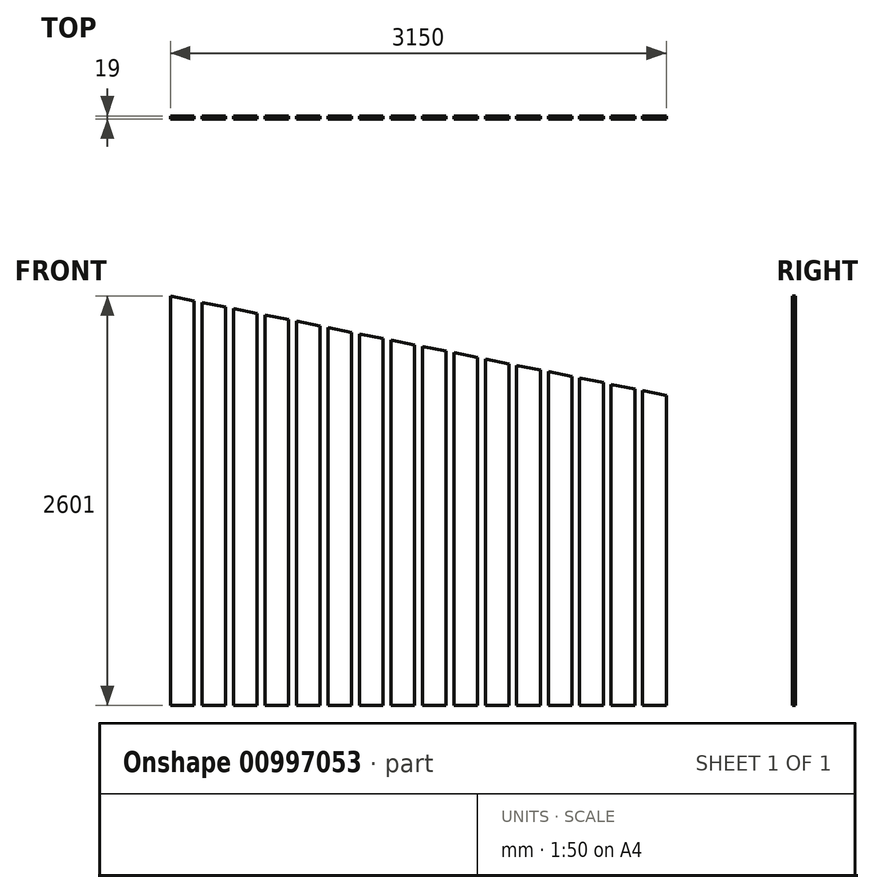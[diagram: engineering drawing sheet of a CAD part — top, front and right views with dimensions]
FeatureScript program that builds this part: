
annotation { "Feature Type Name" : "Feature", "Feature Type Description" : "" }
export const myFeature = defineFeature(function(context is Context, id is Id, definition is map)
    precondition{}
    {
        {
            var Q0;
            Q0=qCreatedBy(makeId("Top.planeOp"),FACE);
            var sketch = newSketch(context, id + "F0", { "sketchPlane" : qUnion([Q0])});
            skLineSegment(sketch, "E0.bottom", {"start": v(0, 0) * mm, "end": v(-150, 0) * mm});
            skLineSegment(sketch, "E0.top", {"start": v(0, 19) * mm, "end": v(-150, 19) * mm});
            skLineSegment(sketch, "E0.left", {"start": v(0, 0) * mm, "end": v(0, 19) * mm});
            skLineSegment(sketch, "E0.right", {"start": v(-150, 0) * mm, "end": v(-150, 19) * mm});
            skSolve(sketch);
        }
        {
            var Q0;
            Q0=makeQuery(id+"F0.imprint","IMPRINT",FACE,{"disambiguationData":[TD([[makeQuery(id+"F0.imprint","IMPRINT",EDGE,{"derivedFrom":sQuery(id+"F0.wireOp",EDGE,"E0.bottom")}),-1.0]])]});
            extrude(context, id + "F1", {"entities" : qUnion([Q0]), "depth" : 2000 * mm, "offsetDistance" : 25 * mm});
        }
        {
            var Q0;
            Q0=makeQuery(id+"F1.opExtrude","CAP_EDGE",EDGE,{"disambiguationData":[OSD([sQuery(id+"F0.wireOp",EDGE,"E0.left")])],"isStart":false});
            chamfer(context, id + "F2", {"entities" : qUnion([Q0]), "chamferType" : ChamferType.OFFSET_ANGLE, "width" : 150 * mm, "oppositeDirection" : false, "angle" : 11.3 * degree, "tangentPropagation" : true});
        }
        {
            var Q0;
            Q0=makeQuery(id+"F1.opExtrude","SWEPT_BODY",BODY,{"disambiguationData":[OSD([sQuery(id+"F0.wireOp",EDGE,"E0.bottom"),sQuery(id+"F0.wireOp",EDGE,"E0.top"),sQuery(id+"F0.wireOp",EDGE,"E0.left"),sQuery(id+"F0.wireOp",EDGE,"E0.right")])]});
            transform(context, id + "F3", {"entities" : qUnion([Q0]), "transformType" : TransformType.TRANSLATION_3D, "dx" : -200 * mm, "dy" : 0 * mm, "dz" : 40 * mm, "makeCopy" : true});
        }
        {
            var Q0;
            Q0=makeQuery(id+"F3.opPattern","COPY",BODY,{"derivedFrom":makeQuery(id+"F1.opExtrude","SWEPT_BODY",BODY,{"disambiguationData":[OSD([sQuery(id+"F0.wireOp",EDGE,"E0.bottom"),sQuery(id+"F0.wireOp",EDGE,"E0.top"),sQuery(id+"F0.wireOp",EDGE,"E0.left"),sQuery(id+"F0.wireOp",EDGE,"E0.right")])]}),"instanceName":"1"});
            transform(context, id + "F4", {"entities" : qUnion([Q0]), "transformType" : TransformType.TRANSLATION_3D, "dx" : -200 * mm, "dy" : 0 * mm, "dz" : 41 * mm, "makeCopy" : true});
        }
        {
            var Q0;
            Q0=makeQuery(id+"F4.opPattern","COPY",BODY,{"derivedFrom":makeQuery(id+"F3.opPattern","COPY",BODY,{"derivedFrom":makeQuery(id+"F1.opExtrude","SWEPT_BODY",BODY,{"disambiguationData":[OSD([sQuery(id+"F0.wireOp",EDGE,"E0.bottom"),sQuery(id+"F0.wireOp",EDGE,"E0.top"),sQuery(id+"F0.wireOp",EDGE,"E0.left"),sQuery(id+"F0.wireOp",EDGE,"E0.right")])]}),"instanceName":"1"}),"instanceName":"1"});
            transform(context, id + "F5", {"entities" : qUnion([Q0]), "transformType" : TransformType.TRANSLATION_3D, "dx" : -200 * mm, "dy" : 0 * mm, "dz" : 40 * mm, "makeCopy" : true});
        }
        {
            var Q0;
            Q0=makeQuery(id+"F5.opPattern","COPY",BODY,{"derivedFrom":makeQuery(id+"F4.opPattern","COPY",BODY,{"derivedFrom":makeQuery(id+"F3.opPattern","COPY",BODY,{"derivedFrom":makeQuery(id+"F1.opExtrude","SWEPT_BODY",BODY,{"disambiguationData":[OSD([sQuery(id+"F0.wireOp",EDGE,"E0.bottom"),sQuery(id+"F0.wireOp",EDGE,"E0.top"),sQuery(id+"F0.wireOp",EDGE,"E0.left"),sQuery(id+"F0.wireOp",EDGE,"E0.right")])]}),"instanceName":"1"}),"instanceName":"1"}),"instanceName":"1"});
            transform(context, id + "F6", {"entities" : qUnion([Q0]), "transformType" : TransformType.TRANSLATION_3D, "dx" : -200 * mm, "dy" : 0 * mm, "dz" : 40 * mm, "makeCopy" : true});
        }
        {
            var Q0;
            Q0=makeQuery(id+"F6.opPattern","COPY",BODY,{"derivedFrom":makeQuery(id+"F5.opPattern","COPY",BODY,{"derivedFrom":makeQuery(id+"F4.opPattern","COPY",BODY,{"derivedFrom":makeQuery(id+"F3.opPattern","COPY",BODY,{"derivedFrom":makeQuery(id+"F1.opExtrude","SWEPT_BODY",BODY,{"disambiguationData":[OSD([sQuery(id+"F0.wireOp",EDGE,"E0.bottom"),sQuery(id+"F0.wireOp",EDGE,"E0.top"),sQuery(id+"F0.wireOp",EDGE,"E0.left"),sQuery(id+"F0.wireOp",EDGE,"E0.right")])]}),"instanceName":"1"}),"instanceName":"1"}),"instanceName":"1"}),"instanceName":"1"});
            transform(context, id + "F7", {"entities" : qUnion([Q0]), "transformType" : TransformType.TRANSLATION_3D, "dx" : -200 * mm, "dy" : 0 * mm, "dz" : 40 * mm, "makeCopy" : true});
        }
        {
            var Q0;
            Q0=makeQuery(id+"F7.opPattern","COPY",BODY,{"derivedFrom":makeQuery(id+"F6.opPattern","COPY",BODY,{"derivedFrom":makeQuery(id+"F5.opPattern","COPY",BODY,{"derivedFrom":makeQuery(id+"F4.opPattern","COPY",BODY,{"derivedFrom":makeQuery(id+"F3.opPattern","COPY",BODY,{"derivedFrom":makeQuery(id+"F1.opExtrude","SWEPT_BODY",BODY,{"disambiguationData":[OSD([sQuery(id+"F0.wireOp",EDGE,"E0.bottom"),sQuery(id+"F0.wireOp",EDGE,"E0.top"),sQuery(id+"F0.wireOp",EDGE,"E0.left"),sQuery(id+"F0.wireOp",EDGE,"E0.right")])]}),"instanceName":"1"}),"instanceName":"1"}),"instanceName":"1"}),"instanceName":"1"}),"instanceName":"1"});
            transform(context, id + "F8", {"entities" : qUnion([Q0]), "transformType" : TransformType.TRANSLATION_3D, "dx" : -200 * mm, "dy" : 0 * mm, "dz" : 40 * mm, "makeCopy" : true});
        }
        {
            var Q0;
            Q0=makeQuery(id+"F8.opPattern","COPY",BODY,{"derivedFrom":makeQuery(id+"F7.opPattern","COPY",BODY,{"derivedFrom":makeQuery(id+"F6.opPattern","COPY",BODY,{"derivedFrom":makeQuery(id+"F5.opPattern","COPY",BODY,{"derivedFrom":makeQuery(id+"F4.opPattern","COPY",BODY,{"derivedFrom":makeQuery(id+"F3.opPattern","COPY",BODY,{"derivedFrom":makeQuery(id+"F1.opExtrude","SWEPT_BODY",BODY,{"disambiguationData":[OSD([sQuery(id+"F0.wireOp",EDGE,"E0.bottom"),sQuery(id+"F0.wireOp",EDGE,"E0.top"),sQuery(id+"F0.wireOp",EDGE,"E0.left"),sQuery(id+"F0.wireOp",EDGE,"E0.right")])]}),"instanceName":"1"}),"instanceName":"1"}),"instanceName":"1"}),"instanceName":"1"}),"instanceName":"1"}),"instanceName":"1"});
            transform(context, id + "F9", {"entities" : qUnion([Q0]), "transformType" : TransformType.TRANSLATION_3D, "dx" : -200 * mm, "dy" : 0 * mm, "dz" : 40 * mm, "makeCopy" : true});
        }
        {
            var Q0;
            Q0=makeQuery(id+"F9.opPattern","COPY",BODY,{"derivedFrom":makeQuery(id+"F8.opPattern","COPY",BODY,{"derivedFrom":makeQuery(id+"F7.opPattern","COPY",BODY,{"derivedFrom":makeQuery(id+"F6.opPattern","COPY",BODY,{"derivedFrom":makeQuery(id+"F5.opPattern","COPY",BODY,{"derivedFrom":makeQuery(id+"F4.opPattern","COPY",BODY,{"derivedFrom":makeQuery(id+"F3.opPattern","COPY",BODY,{"derivedFrom":makeQuery(id+"F1.opExtrude","SWEPT_BODY",BODY,{"disambiguationData":[OSD([sQuery(id+"F0.wireOp",EDGE,"E0.bottom"),sQuery(id+"F0.wireOp",EDGE,"E0.top"),sQuery(id+"F0.wireOp",EDGE,"E0.left"),sQuery(id+"F0.wireOp",EDGE,"E0.right")])]}),"instanceName":"1"}),"instanceName":"1"}),"instanceName":"1"}),"instanceName":"1"}),"instanceName":"1"}),"instanceName":"1"}),"instanceName":"1"});
            transform(context, id + "F10", {"entities" : qUnion([Q0]), "transformType" : TransformType.TRANSLATION_3D, "dx" : -200 * mm, "dy" : 0 * mm, "dz" : 40 * mm, "makeCopy" : true});
        }
        {
            var Q0;
            Q0=makeQuery(id+"F10.opPattern","COPY",BODY,{"derivedFrom":makeQuery(id+"F9.opPattern","COPY",BODY,{"derivedFrom":makeQuery(id+"F8.opPattern","COPY",BODY,{"derivedFrom":makeQuery(id+"F7.opPattern","COPY",BODY,{"derivedFrom":makeQuery(id+"F6.opPattern","COPY",BODY,{"derivedFrom":makeQuery(id+"F5.opPattern","COPY",BODY,{"derivedFrom":makeQuery(id+"F4.opPattern","COPY",BODY,{"derivedFrom":makeQuery(id+"F3.opPattern","COPY",BODY,{"derivedFrom":makeQuery(id+"F1.opExtrude","SWEPT_BODY",BODY,{"disambiguationData":[OSD([sQuery(id+"F0.wireOp",EDGE,"E0.bottom"),sQuery(id+"F0.wireOp",EDGE,"E0.top"),sQuery(id+"F0.wireOp",EDGE,"E0.left"),sQuery(id+"F0.wireOp",EDGE,"E0.right")])]}),"instanceName":"1"}),"instanceName":"1"}),"instanceName":"1"}),"instanceName":"1"}),"instanceName":"1"}),"instanceName":"1"}),"instanceName":"1"}),"instanceName":"1"});
            transform(context, id + "F11", {"entities" : qUnion([Q0]), "transformType" : TransformType.TRANSLATION_3D, "dx" : -200 * mm, "dy" : 0 * mm, "dz" : 40 * mm, "makeCopy" : true});
        }
        {
            var Q0;
            Q0=makeQuery(id+"F11.opPattern","COPY",BODY,{"derivedFrom":makeQuery(id+"F10.opPattern","COPY",BODY,{"derivedFrom":makeQuery(id+"F9.opPattern","COPY",BODY,{"derivedFrom":makeQuery(id+"F8.opPattern","COPY",BODY,{"derivedFrom":makeQuery(id+"F7.opPattern","COPY",BODY,{"derivedFrom":makeQuery(id+"F6.opPattern","COPY",BODY,{"derivedFrom":makeQuery(id+"F5.opPattern","COPY",BODY,{"derivedFrom":makeQuery(id+"F4.opPattern","COPY",BODY,{"derivedFrom":makeQuery(id+"F3.opPattern","COPY",BODY,{"derivedFrom":makeQuery(id+"F1.opExtrude","SWEPT_BODY",BODY,{"disambiguationData":[OSD([sQuery(id+"F0.wireOp",EDGE,"E0.bottom"),sQuery(id+"F0.wireOp",EDGE,"E0.top"),sQuery(id+"F0.wireOp",EDGE,"E0.left"),sQuery(id+"F0.wireOp",EDGE,"E0.right")])]}),"instanceName":"1"}),"instanceName":"1"}),"instanceName":"1"}),"instanceName":"1"}),"instanceName":"1"}),"instanceName":"1"}),"instanceName":"1"}),"instanceName":"1"}),"instanceName":"1"});
            transform(context, id + "F12", {"entities" : qUnion([Q0]), "transformType" : TransformType.TRANSLATION_3D, "dx" : -200 * mm, "dy" : 0 * mm, "dz" : 40 * mm, "makeCopy" : true});
        }
        {
            var Q0;
            Q0=makeQuery(id+"F12.opPattern","COPY",BODY,{"derivedFrom":makeQuery(id+"F11.opPattern","COPY",BODY,{"derivedFrom":makeQuery(id+"F10.opPattern","COPY",BODY,{"derivedFrom":makeQuery(id+"F9.opPattern","COPY",BODY,{"derivedFrom":makeQuery(id+"F8.opPattern","COPY",BODY,{"derivedFrom":makeQuery(id+"F7.opPattern","COPY",BODY,{"derivedFrom":makeQuery(id+"F6.opPattern","COPY",BODY,{"derivedFrom":makeQuery(id+"F5.opPattern","COPY",BODY,{"derivedFrom":makeQuery(id+"F4.opPattern","COPY",BODY,{"derivedFrom":makeQuery(id+"F3.opPattern","COPY",BODY,{"derivedFrom":makeQuery(id+"F1.opExtrude","SWEPT_BODY",BODY,{"disambiguationData":[OSD([sQuery(id+"F0.wireOp",EDGE,"E0.bottom"),sQuery(id+"F0.wireOp",EDGE,"E0.top"),sQuery(id+"F0.wireOp",EDGE,"E0.left"),sQuery(id+"F0.wireOp",EDGE,"E0.right")])]}),"instanceName":"1"}),"instanceName":"1"}),"instanceName":"1"}),"instanceName":"1"}),"instanceName":"1"}),"instanceName":"1"}),"instanceName":"1"}),"instanceName":"1"}),"instanceName":"1"}),"instanceName":"1"});
            transform(context, id + "F13", {"entities" : qUnion([Q0]), "transformType" : TransformType.TRANSLATION_3D, "dx" : -200 * mm, "dy" : 0 * mm, "dz" : 40 * mm, "makeCopy" : true});
        }
        {
            var Q0;
            Q0=makeQuery(id+"F3.opPattern","COPY",FACE,{"derivedFrom":makeQuery(id+"F1.opExtrude","CAP_FACE",FACE,{"disambiguationData":[OSD([sQuery(id+"F0.wireOp",EDGE,"E0.bottom"),sQuery(id+"F0.wireOp",EDGE,"E0.top"),sQuery(id+"F0.wireOp",EDGE,"E0.left"),sQuery(id+"F0.wireOp",EDGE,"E0.right")])],"isStart":true}),"instanceName":"1"});
            extrude(context, id + "F14", {"entities" : qUnion([Q0]), "operationType" : NewBodyOperationType.ADD, "depth" : 40 * mm, "offsetDistance" : 25 * mm});
        }
        {
            var Q0;
            Q0=makeQuery(id+"F5.opPattern","COPY",FACE,{"derivedFrom":makeQuery(id+"F4.opPattern","COPY",FACE,{"derivedFrom":makeQuery(id+"F3.opPattern","COPY",FACE,{"derivedFrom":makeQuery(id+"F1.opExtrude","CAP_FACE",FACE,{"disambiguationData":[OSD([sQuery(id+"F0.wireOp",EDGE,"E0.bottom"),sQuery(id+"F0.wireOp",EDGE,"E0.top"),sQuery(id+"F0.wireOp",EDGE,"E0.left"),sQuery(id+"F0.wireOp",EDGE,"E0.right")])],"isStart":true}),"instanceName":"1"}),"instanceName":"1"}),"instanceName":"1"});
            extrude(context, id + "F15", {"entities" : qUnion([Q0]), "operationType" : NewBodyOperationType.ADD, "depth" : 120 * mm, "offsetDistance" : 25 * mm});
        }
        {
            var Q0;
            Q0=makeQuery(id+"F4.opPattern","COPY",FACE,{"derivedFrom":makeQuery(id+"F3.opPattern","COPY",FACE,{"derivedFrom":makeQuery(id+"F1.opExtrude","CAP_FACE",FACE,{"disambiguationData":[OSD([sQuery(id+"F0.wireOp",EDGE,"E0.bottom"),sQuery(id+"F0.wireOp",EDGE,"E0.top"),sQuery(id+"F0.wireOp",EDGE,"E0.left"),sQuery(id+"F0.wireOp",EDGE,"E0.right")])],"isStart":true}),"instanceName":"1"}),"instanceName":"1"});
            extrude(context, id + "F16", {"entities" : qUnion([Q0]), "operationType" : NewBodyOperationType.ADD, "depth" : 80 * mm, "offsetDistance" : 25 * mm});
        }
        {
            var Q0;
            Q0=makeQuery(id+"F6.opPattern","COPY",FACE,{"derivedFrom":makeQuery(id+"F5.opPattern","COPY",FACE,{"derivedFrom":makeQuery(id+"F4.opPattern","COPY",FACE,{"derivedFrom":makeQuery(id+"F3.opPattern","COPY",FACE,{"derivedFrom":makeQuery(id+"F1.opExtrude","CAP_FACE",FACE,{"disambiguationData":[OSD([sQuery(id+"F0.wireOp",EDGE,"E0.bottom"),sQuery(id+"F0.wireOp",EDGE,"E0.top"),sQuery(id+"F0.wireOp",EDGE,"E0.left"),sQuery(id+"F0.wireOp",EDGE,"E0.right")])],"isStart":true}),"instanceName":"1"}),"instanceName":"1"}),"instanceName":"1"}),"instanceName":"1"});
            extrude(context, id + "F17", {"entities" : qUnion([Q0]), "operationType" : NewBodyOperationType.ADD, "depth" : 160 * mm, "offsetDistance" : 25 * mm});
        }
        {
            var Q0;
            Q0=makeQuery(id+"F7.opPattern","COPY",FACE,{"derivedFrom":makeQuery(id+"F6.opPattern","COPY",FACE,{"derivedFrom":makeQuery(id+"F5.opPattern","COPY",FACE,{"derivedFrom":makeQuery(id+"F4.opPattern","COPY",FACE,{"derivedFrom":makeQuery(id+"F3.opPattern","COPY",FACE,{"derivedFrom":makeQuery(id+"F1.opExtrude","CAP_FACE",FACE,{"disambiguationData":[OSD([sQuery(id+"F0.wireOp",EDGE,"E0.bottom"),sQuery(id+"F0.wireOp",EDGE,"E0.top"),sQuery(id+"F0.wireOp",EDGE,"E0.left"),sQuery(id+"F0.wireOp",EDGE,"E0.right")])],"isStart":true}),"instanceName":"1"}),"instanceName":"1"}),"instanceName":"1"}),"instanceName":"1"}),"instanceName":"1"});
            extrude(context, id + "F18", {"entities" : qUnion([Q0]), "operationType" : NewBodyOperationType.ADD, "depth" : 200 * mm, "offsetDistance" : 25 * mm});
        }
        {
            var Q0;
            Q0=makeQuery(id+"F8.opPattern","COPY",FACE,{"derivedFrom":makeQuery(id+"F7.opPattern","COPY",FACE,{"derivedFrom":makeQuery(id+"F6.opPattern","COPY",FACE,{"derivedFrom":makeQuery(id+"F5.opPattern","COPY",FACE,{"derivedFrom":makeQuery(id+"F4.opPattern","COPY",FACE,{"derivedFrom":makeQuery(id+"F3.opPattern","COPY",FACE,{"derivedFrom":makeQuery(id+"F1.opExtrude","CAP_FACE",FACE,{"disambiguationData":[OSD([sQuery(id+"F0.wireOp",EDGE,"E0.bottom"),sQuery(id+"F0.wireOp",EDGE,"E0.top"),sQuery(id+"F0.wireOp",EDGE,"E0.left"),sQuery(id+"F0.wireOp",EDGE,"E0.right")])],"isStart":true}),"instanceName":"1"}),"instanceName":"1"}),"instanceName":"1"}),"instanceName":"1"}),"instanceName":"1"}),"instanceName":"1"});
            extrude(context, id + "F19", {"entities" : qUnion([Q0]), "operationType" : NewBodyOperationType.ADD, "depth" : 240 * mm, "offsetDistance" : 25 * mm});
        }
        {
            var Q0;
            Q0=makeQuery(id+"F9.opPattern","COPY",FACE,{"derivedFrom":makeQuery(id+"F8.opPattern","COPY",FACE,{"derivedFrom":makeQuery(id+"F7.opPattern","COPY",FACE,{"derivedFrom":makeQuery(id+"F6.opPattern","COPY",FACE,{"derivedFrom":makeQuery(id+"F5.opPattern","COPY",FACE,{"derivedFrom":makeQuery(id+"F4.opPattern","COPY",FACE,{"derivedFrom":makeQuery(id+"F3.opPattern","COPY",FACE,{"derivedFrom":makeQuery(id+"F1.opExtrude","CAP_FACE",FACE,{"disambiguationData":[OSD([sQuery(id+"F0.wireOp",EDGE,"E0.bottom"),sQuery(id+"F0.wireOp",EDGE,"E0.top"),sQuery(id+"F0.wireOp",EDGE,"E0.left"),sQuery(id+"F0.wireOp",EDGE,"E0.right")])],"isStart":true}),"instanceName":"1"}),"instanceName":"1"}),"instanceName":"1"}),"instanceName":"1"}),"instanceName":"1"}),"instanceName":"1"}),"instanceName":"1"});
            extrude(context, id + "F20", {"entities" : qUnion([Q0]), "operationType" : NewBodyOperationType.ADD, "depth" : 280 * mm, "offsetDistance" : 25 * mm});
        }
        {
            var Q0;
            Q0=makeQuery(id+"F10.opPattern","COPY",FACE,{"derivedFrom":makeQuery(id+"F9.opPattern","COPY",FACE,{"derivedFrom":makeQuery(id+"F8.opPattern","COPY",FACE,{"derivedFrom":makeQuery(id+"F7.opPattern","COPY",FACE,{"derivedFrom":makeQuery(id+"F6.opPattern","COPY",FACE,{"derivedFrom":makeQuery(id+"F5.opPattern","COPY",FACE,{"derivedFrom":makeQuery(id+"F4.opPattern","COPY",FACE,{"derivedFrom":makeQuery(id+"F3.opPattern","COPY",FACE,{"derivedFrom":makeQuery(id+"F1.opExtrude","CAP_FACE",FACE,{"disambiguationData":[OSD([sQuery(id+"F0.wireOp",EDGE,"E0.bottom"),sQuery(id+"F0.wireOp",EDGE,"E0.top"),sQuery(id+"F0.wireOp",EDGE,"E0.left"),sQuery(id+"F0.wireOp",EDGE,"E0.right")])],"isStart":true}),"instanceName":"1"}),"instanceName":"1"}),"instanceName":"1"}),"instanceName":"1"}),"instanceName":"1"}),"instanceName":"1"}),"instanceName":"1"}),"instanceName":"1"});
            extrude(context, id + "F21", {"entities" : qUnion([Q0]), "operationType" : NewBodyOperationType.ADD, "depth" : 320 * mm, "offsetDistance" : 25 * mm});
        }
        {
            var Q0;
            Q0=makeQuery(id+"F11.opPattern","COPY",FACE,{"derivedFrom":makeQuery(id+"F10.opPattern","COPY",FACE,{"derivedFrom":makeQuery(id+"F9.opPattern","COPY",FACE,{"derivedFrom":makeQuery(id+"F8.opPattern","COPY",FACE,{"derivedFrom":makeQuery(id+"F7.opPattern","COPY",FACE,{"derivedFrom":makeQuery(id+"F6.opPattern","COPY",FACE,{"derivedFrom":makeQuery(id+"F5.opPattern","COPY",FACE,{"derivedFrom":makeQuery(id+"F4.opPattern","COPY",FACE,{"derivedFrom":makeQuery(id+"F3.opPattern","COPY",FACE,{"derivedFrom":makeQuery(id+"F1.opExtrude","CAP_FACE",FACE,{"disambiguationData":[OSD([sQuery(id+"F0.wireOp",EDGE,"E0.bottom"),sQuery(id+"F0.wireOp",EDGE,"E0.top"),sQuery(id+"F0.wireOp",EDGE,"E0.left"),sQuery(id+"F0.wireOp",EDGE,"E0.right")])],"isStart":true}),"instanceName":"1"}),"instanceName":"1"}),"instanceName":"1"}),"instanceName":"1"}),"instanceName":"1"}),"instanceName":"1"}),"instanceName":"1"}),"instanceName":"1"}),"instanceName":"1"});
            extrude(context, id + "F22", {"entities" : qUnion([Q0]), "operationType" : NewBodyOperationType.ADD, "depth" : 360 * mm, "offsetDistance" : 25 * mm});
        }
        {
            var Q0;
            Q0=makeQuery(id+"F12.opPattern","COPY",FACE,{"derivedFrom":makeQuery(id+"F11.opPattern","COPY",FACE,{"derivedFrom":makeQuery(id+"F10.opPattern","COPY",FACE,{"derivedFrom":makeQuery(id+"F9.opPattern","COPY",FACE,{"derivedFrom":makeQuery(id+"F8.opPattern","COPY",FACE,{"derivedFrom":makeQuery(id+"F7.opPattern","COPY",FACE,{"derivedFrom":makeQuery(id+"F6.opPattern","COPY",FACE,{"derivedFrom":makeQuery(id+"F5.opPattern","COPY",FACE,{"derivedFrom":makeQuery(id+"F4.opPattern","COPY",FACE,{"derivedFrom":makeQuery(id+"F3.opPattern","COPY",FACE,{"derivedFrom":makeQuery(id+"F1.opExtrude","CAP_FACE",FACE,{"disambiguationData":[OSD([sQuery(id+"F0.wireOp",EDGE,"E0.bottom"),sQuery(id+"F0.wireOp",EDGE,"E0.top"),sQuery(id+"F0.wireOp",EDGE,"E0.left"),sQuery(id+"F0.wireOp",EDGE,"E0.right")])],"isStart":true}),"instanceName":"1"}),"instanceName":"1"}),"instanceName":"1"}),"instanceName":"1"}),"instanceName":"1"}),"instanceName":"1"}),"instanceName":"1"}),"instanceName":"1"}),"instanceName":"1"}),"instanceName":"1"});
            extrude(context, id + "F23", {"entities" : qUnion([Q0]), "operationType" : NewBodyOperationType.ADD, "depth" : 400 * mm, "offsetDistance" : 25 * mm});
        }
        {
            var Q0;
            Q0=makeQuery(id+"F13.opPattern","COPY",FACE,{"derivedFrom":makeQuery(id+"F12.opPattern","COPY",FACE,{"derivedFrom":makeQuery(id+"F11.opPattern","COPY",FACE,{"derivedFrom":makeQuery(id+"F10.opPattern","COPY",FACE,{"derivedFrom":makeQuery(id+"F9.opPattern","COPY",FACE,{"derivedFrom":makeQuery(id+"F8.opPattern","COPY",FACE,{"derivedFrom":makeQuery(id+"F7.opPattern","COPY",FACE,{"derivedFrom":makeQuery(id+"F6.opPattern","COPY",FACE,{"derivedFrom":makeQuery(id+"F5.opPattern","COPY",FACE,{"derivedFrom":makeQuery(id+"F4.opPattern","COPY",FACE,{"derivedFrom":makeQuery(id+"F3.opPattern","COPY",FACE,{"derivedFrom":makeQuery(id+"F1.opExtrude","CAP_FACE",FACE,{"disambiguationData":[OSD([sQuery(id+"F0.wireOp",EDGE,"E0.bottom"),sQuery(id+"F0.wireOp",EDGE,"E0.top"),sQuery(id+"F0.wireOp",EDGE,"E0.left"),sQuery(id+"F0.wireOp",EDGE,"E0.right")])],"isStart":true}),"instanceName":"1"}),"instanceName":"1"}),"instanceName":"1"}),"instanceName":"1"}),"instanceName":"1"}),"instanceName":"1"}),"instanceName":"1"}),"instanceName":"1"}),"instanceName":"1"}),"instanceName":"1"}),"instanceName":"1"});
            extrude(context, id + "F24", {"entities" : qUnion([Q0]), "operationType" : NewBodyOperationType.ADD, "depth" : 440 * mm, "offsetDistance" : 25 * mm});
        }
        {
            var Q0;
            Q0=makeQuery(id+"F13.opPattern","COPY",BODY,{"derivedFrom":makeQuery(id+"F12.opPattern","COPY",BODY,{"derivedFrom":makeQuery(id+"F11.opPattern","COPY",BODY,{"derivedFrom":makeQuery(id+"F10.opPattern","COPY",BODY,{"derivedFrom":makeQuery(id+"F9.opPattern","COPY",BODY,{"derivedFrom":makeQuery(id+"F8.opPattern","COPY",BODY,{"derivedFrom":makeQuery(id+"F7.opPattern","COPY",BODY,{"derivedFrom":makeQuery(id+"F6.opPattern","COPY",BODY,{"derivedFrom":makeQuery(id+"F5.opPattern","COPY",BODY,{"derivedFrom":makeQuery(id+"F4.opPattern","COPY",BODY,{"derivedFrom":makeQuery(id+"F3.opPattern","COPY",BODY,{"derivedFrom":makeQuery(id+"F1.opExtrude","SWEPT_BODY",BODY,{"disambiguationData":[OSD([sQuery(id+"F0.wireOp",EDGE,"E0.bottom"),sQuery(id+"F0.wireOp",EDGE,"E0.top"),sQuery(id+"F0.wireOp",EDGE,"E0.left"),sQuery(id+"F0.wireOp",EDGE,"E0.right")])]}),"instanceName":"1"}),"instanceName":"1"}),"instanceName":"1"}),"instanceName":"1"}),"instanceName":"1"}),"instanceName":"1"}),"instanceName":"1"}),"instanceName":"1"}),"instanceName":"1"}),"instanceName":"1"}),"instanceName":"1"});
            transform(context, id + "F25", {"entities" : qUnion([Q0]), "transformType" : TransformType.TRANSLATION_3D, "dx" : -200 * mm, "dy" : 0 * mm, "dz" : 40 * mm, "makeCopy" : true});
        }
        {
            var Q0;
            Q0=makeQuery(id+"F25.opPattern","COPY",BODY,{"derivedFrom":makeQuery(id+"F13.opPattern","COPY",BODY,{"derivedFrom":makeQuery(id+"F12.opPattern","COPY",BODY,{"derivedFrom":makeQuery(id+"F11.opPattern","COPY",BODY,{"derivedFrom":makeQuery(id+"F10.opPattern","COPY",BODY,{"derivedFrom":makeQuery(id+"F9.opPattern","COPY",BODY,{"derivedFrom":makeQuery(id+"F8.opPattern","COPY",BODY,{"derivedFrom":makeQuery(id+"F7.opPattern","COPY",BODY,{"derivedFrom":makeQuery(id+"F6.opPattern","COPY",BODY,{"derivedFrom":makeQuery(id+"F5.opPattern","COPY",BODY,{"derivedFrom":makeQuery(id+"F4.opPattern","COPY",BODY,{"derivedFrom":makeQuery(id+"F3.opPattern","COPY",BODY,{"derivedFrom":makeQuery(id+"F1.opExtrude","SWEPT_BODY",BODY,{"disambiguationData":[OSD([sQuery(id+"F0.wireOp",EDGE,"E0.bottom"),sQuery(id+"F0.wireOp",EDGE,"E0.top"),sQuery(id+"F0.wireOp",EDGE,"E0.left"),sQuery(id+"F0.wireOp",EDGE,"E0.right")])]}),"instanceName":"1"}),"instanceName":"1"}),"instanceName":"1"}),"instanceName":"1"}),"instanceName":"1"}),"instanceName":"1"}),"instanceName":"1"}),"instanceName":"1"}),"instanceName":"1"}),"instanceName":"1"}),"instanceName":"1"}),"instanceName":"1"});
            transform(context, id + "F26", {"entities" : qUnion([Q0]), "transformType" : TransformType.TRANSLATION_3D, "dx" : -200 * mm, "dy" : 0 * mm, "dz" : 40 * mm, "makeCopy" : true});
        }
        {
            var Q0;
            Q0=makeQuery(id+"F26.opPattern","COPY",BODY,{"derivedFrom":makeQuery(id+"F25.opPattern","COPY",BODY,{"derivedFrom":makeQuery(id+"F13.opPattern","COPY",BODY,{"derivedFrom":makeQuery(id+"F12.opPattern","COPY",BODY,{"derivedFrom":makeQuery(id+"F11.opPattern","COPY",BODY,{"derivedFrom":makeQuery(id+"F10.opPattern","COPY",BODY,{"derivedFrom":makeQuery(id+"F9.opPattern","COPY",BODY,{"derivedFrom":makeQuery(id+"F8.opPattern","COPY",BODY,{"derivedFrom":makeQuery(id+"F7.opPattern","COPY",BODY,{"derivedFrom":makeQuery(id+"F6.opPattern","COPY",BODY,{"derivedFrom":makeQuery(id+"F5.opPattern","COPY",BODY,{"derivedFrom":makeQuery(id+"F4.opPattern","COPY",BODY,{"derivedFrom":makeQuery(id+"F3.opPattern","COPY",BODY,{"derivedFrom":makeQuery(id+"F1.opExtrude","SWEPT_BODY",BODY,{"disambiguationData":[OSD([sQuery(id+"F0.wireOp",EDGE,"E0.bottom"),sQuery(id+"F0.wireOp",EDGE,"E0.top"),sQuery(id+"F0.wireOp",EDGE,"E0.left"),sQuery(id+"F0.wireOp",EDGE,"E0.right")])]}),"instanceName":"1"}),"instanceName":"1"}),"instanceName":"1"}),"instanceName":"1"}),"instanceName":"1"}),"instanceName":"1"}),"instanceName":"1"}),"instanceName":"1"}),"instanceName":"1"}),"instanceName":"1"}),"instanceName":"1"}),"instanceName":"1"}),"instanceName":"1"});
            transform(context, id + "F27", {"entities" : qUnion([Q0]), "transformType" : TransformType.TRANSLATION_3D, "dx" : -200 * mm, "dy" : 0 * mm, "dz" : 40 * mm, "makeCopy" : true});
        }
        {
            var Q0;
            Q0=makeQuery(id+"F27.opPattern","COPY",BODY,{"derivedFrom":makeQuery(id+"F26.opPattern","COPY",BODY,{"derivedFrom":makeQuery(id+"F25.opPattern","COPY",BODY,{"derivedFrom":makeQuery(id+"F13.opPattern","COPY",BODY,{"derivedFrom":makeQuery(id+"F12.opPattern","COPY",BODY,{"derivedFrom":makeQuery(id+"F11.opPattern","COPY",BODY,{"derivedFrom":makeQuery(id+"F10.opPattern","COPY",BODY,{"derivedFrom":makeQuery(id+"F9.opPattern","COPY",BODY,{"derivedFrom":makeQuery(id+"F8.opPattern","COPY",BODY,{"derivedFrom":makeQuery(id+"F7.opPattern","COPY",BODY,{"derivedFrom":makeQuery(id+"F6.opPattern","COPY",BODY,{"derivedFrom":makeQuery(id+"F5.opPattern","COPY",BODY,{"derivedFrom":makeQuery(id+"F4.opPattern","COPY",BODY,{"derivedFrom":makeQuery(id+"F3.opPattern","COPY",BODY,{"derivedFrom":makeQuery(id+"F1.opExtrude","SWEPT_BODY",BODY,{"disambiguationData":[OSD([sQuery(id+"F0.wireOp",EDGE,"E0.bottom"),sQuery(id+"F0.wireOp",EDGE,"E0.top"),sQuery(id+"F0.wireOp",EDGE,"E0.left"),sQuery(id+"F0.wireOp",EDGE,"E0.right")])]}),"instanceName":"1"}),"instanceName":"1"}),"instanceName":"1"}),"instanceName":"1"}),"instanceName":"1"}),"instanceName":"1"}),"instanceName":"1"}),"instanceName":"1"}),"instanceName":"1"}),"instanceName":"1"}),"instanceName":"1"}),"instanceName":"1"}),"instanceName":"1"}),"instanceName":"1"});
            transform(context, id + "F28", {"entities" : qUnion([Q0]), "transformType" : TransformType.TRANSLATION_3D, "dx" : -200 * mm, "dy" : 0 * mm, "dz" : 40 * mm, "makeCopy" : true});
        }
        {
            var Q0;
            Q0=makeQuery(id+"F25.opPattern","COPY",FACE,{"derivedFrom":makeQuery(id+"F24.opExtrude","CAP_FACE",FACE,{"disambiguationData":[OSD([sQuery(id+"F0.wireOp",EDGE,"E0.bottom"),sQuery(id+"F0.wireOp",EDGE,"E0.top"),sQuery(id+"F0.wireOp",EDGE,"E0.left"),sQuery(id+"F0.wireOp",EDGE,"E0.right")])],"isStart":false}),"instanceName":"1"});
            extrude(context, id + "F29", {"entities" : qUnion([Q0]), "operationType" : NewBodyOperationType.ADD, "depth" : 40 * mm, "offsetDistance" : 25 * mm});
        }
        {
            var Q0;
            Q0=makeQuery(id+"F26.opPattern","COPY",FACE,{"derivedFrom":makeQuery(id+"F25.opPattern","COPY",FACE,{"derivedFrom":makeQuery(id+"F24.opExtrude","CAP_FACE",FACE,{"disambiguationData":[OSD([sQuery(id+"F0.wireOp",EDGE,"E0.bottom"),sQuery(id+"F0.wireOp",EDGE,"E0.top"),sQuery(id+"F0.wireOp",EDGE,"E0.left"),sQuery(id+"F0.wireOp",EDGE,"E0.right")])],"isStart":false}),"instanceName":"1"}),"instanceName":"1"});
            extrude(context, id + "F30", {"entities" : qUnion([Q0]), "operationType" : NewBodyOperationType.ADD, "depth" : 80 * mm, "offsetDistance" : 25 * mm});
        }
        {
            var Q0;
            Q0=makeQuery(id+"F27.opPattern","COPY",FACE,{"derivedFrom":makeQuery(id+"F26.opPattern","COPY",FACE,{"derivedFrom":makeQuery(id+"F25.opPattern","COPY",FACE,{"derivedFrom":makeQuery(id+"F24.opExtrude","CAP_FACE",FACE,{"disambiguationData":[OSD([sQuery(id+"F0.wireOp",EDGE,"E0.bottom"),sQuery(id+"F0.wireOp",EDGE,"E0.top"),sQuery(id+"F0.wireOp",EDGE,"E0.left"),sQuery(id+"F0.wireOp",EDGE,"E0.right")])],"isStart":false}),"instanceName":"1"}),"instanceName":"1"}),"instanceName":"1"});
            extrude(context, id + "F31", {"entities" : qUnion([Q0]), "operationType" : NewBodyOperationType.ADD, "depth" : 120 * mm, "offsetDistance" : 25 * mm});
        }
        {
            var Q0;
            Q0=makeQuery(id+"F28.opPattern","COPY",FACE,{"derivedFrom":makeQuery(id+"F27.opPattern","COPY",FACE,{"derivedFrom":makeQuery(id+"F26.opPattern","COPY",FACE,{"derivedFrom":makeQuery(id+"F25.opPattern","COPY",FACE,{"derivedFrom":makeQuery(id+"F24.opExtrude","CAP_FACE",FACE,{"disambiguationData":[OSD([sQuery(id+"F0.wireOp",EDGE,"E0.bottom"),sQuery(id+"F0.wireOp",EDGE,"E0.top"),sQuery(id+"F0.wireOp",EDGE,"E0.left"),sQuery(id+"F0.wireOp",EDGE,"E0.right")])],"isStart":false}),"instanceName":"1"}),"instanceName":"1"}),"instanceName":"1"}),"instanceName":"1"});
            extrude(context, id + "F32", {"entities" : qUnion([Q0]), "operationType" : NewBodyOperationType.ADD, "depth" : 160 * mm, "offsetDistance" : 25 * mm});
        }
    });
